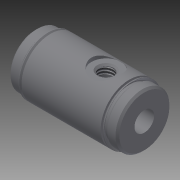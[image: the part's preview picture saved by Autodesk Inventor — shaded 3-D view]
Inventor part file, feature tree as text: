
AUTODESK INVENTOR PART (.ipt)
format: ipt  version: 2014 (Build 180170000, 170)  size: 212,480 bytes
history: native  units: in
note: dims shown in document units (in); Inventor stores cm internally (conversion verified against a paired STEP export)
features: other x49, sketch x5, revolve x4, hole x1, thread x1
ambient origin geometry x8: Origin, YZ Plane, XZ Plane, XY Plane, X Axis, Y Axis, Z Axis, Center Point
bodies: Solid1 (feature_tree)
feature tree (60):
  revolve  "Revolution1"  Angle=360.0deg
  hole  "Hole1"  [1 undecoded]
  revolve  "Revolution2"  [1 undecoded]
  thread  "Thread1"  [1 undecoded]
  revolve  "Revolution3"  [1 undecoded]
  revolve  "Revolution4"  [1 undecoded]
  other  "ba2_XY"
  other  "ba2_YZ"
  other  "ba2_ZX"
  other  "ba2_X"
  other  "ba2_Y"
  other  "ba2_Z"
  other  "ba2_Center"
  other  "centar_XY"
  other  "centar_YZ"
  other  "centar_ZX"
  other  "centar_X"
  other  "centar_Y"
  other  "centar_Z"
  other  "centar_Center"
  other  "d1_XY"
  other  "d1_YZ"
  other  "d1_ZX"
  other  "d1_X"
  other  "d1_Y"
  other  "d1_Z"
  other  "d1_Center"
  other  "d2_XY"
  other  "d2_YZ"
  other  "d2_ZX"
  other  "d2_X"
  other  "d2_Y"
  other  "d2_Z"
  other  "d2_Center"
  other  "to_cyl_A_XY"
  other  "to_cyl_A_YZ"
  other  "to_cyl_A_ZX"
  other  "to_cyl_A_X"
  other  "to_cyl_A_Y"
  other  "to_cyl_A_Z"
  other  "to_cyl_A_Center"
  other  "to_cyl_B_XY"
  other  "to_cyl_B_YZ"
  other  "to_cyl_B_ZX"
  other  "to_cyl_B_X"
  other  "to_cyl_B_Y"
  other  "to_cyl_B_Z"
  other  "to_cyl_B_Center"
  other  "to_rod_A_XY"
  other  "to_rod_A_YZ"
  other  "to_rod_A_ZX"
  other  "to_rod_A_X"
  other  "to_rod_A_Y"
  other  "to_rod_A_Z"
  other  "to_rod_A_Center"
  sketch  "Sketch_1"  dims[d0=360.0deg]
  sketch  "Sketch2"  dims[d1=0.21in d2=0.75in d3=0.375in d4=0.25in d5=0.5635in d6=1.156in d7=0.0in d8=360.0deg]
  sketch  "Sketch_6"  dims[d9=0.0955in d10=0.1018in d11=360.0deg]
  sketch  "Sketch_8"  dims[d12=360.0deg]
  sketch  "Sketch_14"
note: 5 required parameter values undecoded (feature->parameter linkage not recoverable at this tier; creation-order binding heuristic only, values carry confidence <= 0.55)
